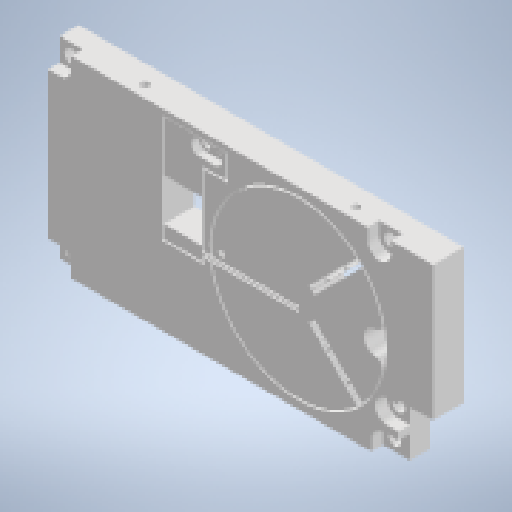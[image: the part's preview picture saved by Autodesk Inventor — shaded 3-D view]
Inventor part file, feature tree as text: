
AUTODESK INVENTOR PART (.ipt)
format: ipt  version: 2023 (Build 270158000, 158)  size: 508,928 bytes
history: native  units: mm
features: extrude x11, sketch x11, other x7, reference x7, fillet x1
ambient origin geometry x8: Origin, YZ Plane, XZ Plane, XY Plane, X Axis, Y Axis, Z Axis, Center Point
bodies: Solid1 (feature_tree)
feature tree (37):
  other  "<userpath>\ClawdDrive\Objet3D\IminaProbe\V3Roue\Settings.xlsx"
  extrude  "Extrusion1"  Depth=9.0mm
  extrude  "Extrusion2"  Depth=9.0mm TaperAngle=0.0deg
  extrude  "Extrusion3"  Depth=40.0mm
  fillet  "Fillet1"  Radius=1.6mm
  extrude  "Extrusion4"  Depth=45.0mm
  extrude  "Extrusion5"  TaperAngle=45.0deg  [1 undecoded]
  extrude  "Extrusion6"  Depth=10.0mm
  extrude  "Extrusion7"  Depth=1.0mm
  extrude  "Extrusion8"  Depth=1.0mm
  extrude  "Extrusion9"  Depth=0.05mm
  extrude  "Extrusion10"  Depth=0.1mm
  extrude  "Extrusion11"  Depth=10.0mm TaperAngle=0.0deg
  sketch  "Sketch1"  dims[d0=8.0mm d1=0.0mm d2=9.0mm]
  reference  "Reference1"
  sketch  "Sketch2"  dims[d3=15.0mm d4=9.0mm d5=0.0mm]
  sketch  "Sketch3"  dims[d6=15.0mm d7=40.0mm d8=1.6mm]
  sketch  "Sketch4"  dims[d9=6.0mm d10=45.0mm]
  sketch  "Sketch5"  dims[d11=20.0mm d12=45.0deg]
  sketch  "Sketch7"  dims[d13=45.0deg d14=10.0mm]
  reference  "Reference2"
  reference  "Reference3"
  sketch  "Sketch8"  dims[d15=46.0mm d16=1.0mm]
  sketch  "Sketch10"  dims[d17=1.0mm d18=1.0mm]
  sketch  "Sketch11"  dims[d19=1.0mm d20=0.05mm]
  sketch  "Sketch12"  dims[d21=0.1mm d22=0.1mm]
  reference  "Reference6"
  reference  "Reference7"
  sketch  "Sketch13"  dims[d23=0.05mm d24=8.0mm d25=0.0mm d26=2.0mm d33=2.65mm d34=0.4mm d35=0.5mm d36=0.5mm d37=20.0mm d38=1.75mm d39=1.6mm d40=25.0mm d41=0.0mm d42=0.5mm d43=0.5mm d44=0.5mm d45=0.5mm d47=1.5mm d48=1.5mm d49=0.1mm d50=0.1mm d51=0.5mm d52=0.5mm d53=0.5mm d54=18.0mm d56=0.0mm d57=1.5mm d58=0.1mm d59=8.0mm d60=0.0mm d61=8.0mm d62=0.0mm d63=16.0mm d64=2.4mm d65=2.4mm d66=8.0mm d67=0.0mm d68=3.0mm d69=14.0mm d70=3.0mm d72=3.0mm d73=3.4mm d74=3.4mm d75=3.4mm d76=3.0mm d77=3.0mm d78=3.0mm d79=4.0mm d80=3.4mm d81=3.0mm d82=3.4mm d83=11.0mm d84=8.0mm d85=0.0mm d86=6.0mm d87=6.0mm d88=6.0mm d89=6.0mm d90=6.0mm d91=3.0mm d92=0.0mm d93=4.0mm d94=4.0mm d95=2.0mm d96=0.0mm d97=7.0mm d98=0.0mm d99=2.05mm d100=2.75mm d101=2.05mm d102=2.05mm d103=2.05mm d104=2.05mm d105=2.05mm d106=7.0mm d107=0.0mm d108=10.0mm d109=23.0mm d110=55.0mm d111=55.0mm d112=2.05mm d113=23.0mm d114=55.0mm d115=7.0mm d116=5.0mm d117=2.0mm d118=5.0mm d119=2.0mm d120=5.0mm d121=2.0mm d122=5.0mm d123=2.0mm d124=11.0mm d125=1.0mm d126=1.0mm d127=2.1mm d128=4.45mm d129=2.0mm d130=2.0mm d131=4.45mm d132=2.1mm]
  reference  "Reference10"
  reference  "Reference11"
  other  "<userpath>\ClawdDrive\Objet3D\IminaProbe\V3Roue\RoueV3.iam"
  other  "RoueV3.iam"
  other  "RoueV3PartB:1"
  other  "AngleScrewBlocActuator:1"
  other  "DifferentialLinearActuator:11"
  other  "DifferentialLinearActuator:12"
note: 1 required parameter value undecoded (feature->parameter linkage not recoverable at this tier; creation-order binding heuristic only, values carry confidence <= 0.55)
